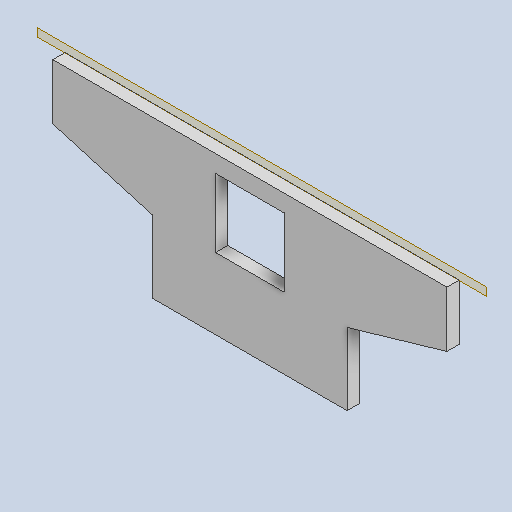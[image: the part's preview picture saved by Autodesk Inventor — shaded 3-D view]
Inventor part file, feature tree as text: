
AUTODESK INVENTOR PART (.ipt)
format: ipt  version: 2023.4 (Build 274418000, 418)  size: 243,712 bytes
history: native  units: mm
features: reference x8, other x6, plane x1, extrude x1, sketch x1
ambient origin geometry x8: Origin, YZ Plane, XZ Plane, XY Plane, X Axis, Y Axis, Z Axis, Center Point
bodies: Solid1 (feature_tree)
feature tree (17):
  plane  "Work Plane1"
  extrude  "Extrusion1"  Depth=0.5mm TaperAngle=0.0deg
  sketch  "Sketch1"  dims[d0=0.3mm d1=0.5mm d2=0.0mm d3=2.8mm d4=2.8mm d5=1.0mm]
  reference  "Reference1"
  reference  "Reference2"
  reference  "Reference3"
  reference  "Reference4"
  reference  "Reference5"
  reference  "Reference6"
  reference  "Reference7"
  reference  "Reference8"
  parser-record x2  (decoder bookkeeping rows leaked as tree rows — omitted from the tree; the rows remain in map.json)
  other  "np1_full_assembly.iam"
  other  "np1_cap_with_headstage:1"
  other  "full_assembly.iam"
  other  "cap_with_headstage:1"
note: 2 file-system paths scrubbed to <path> (originals preserved in map.json)
